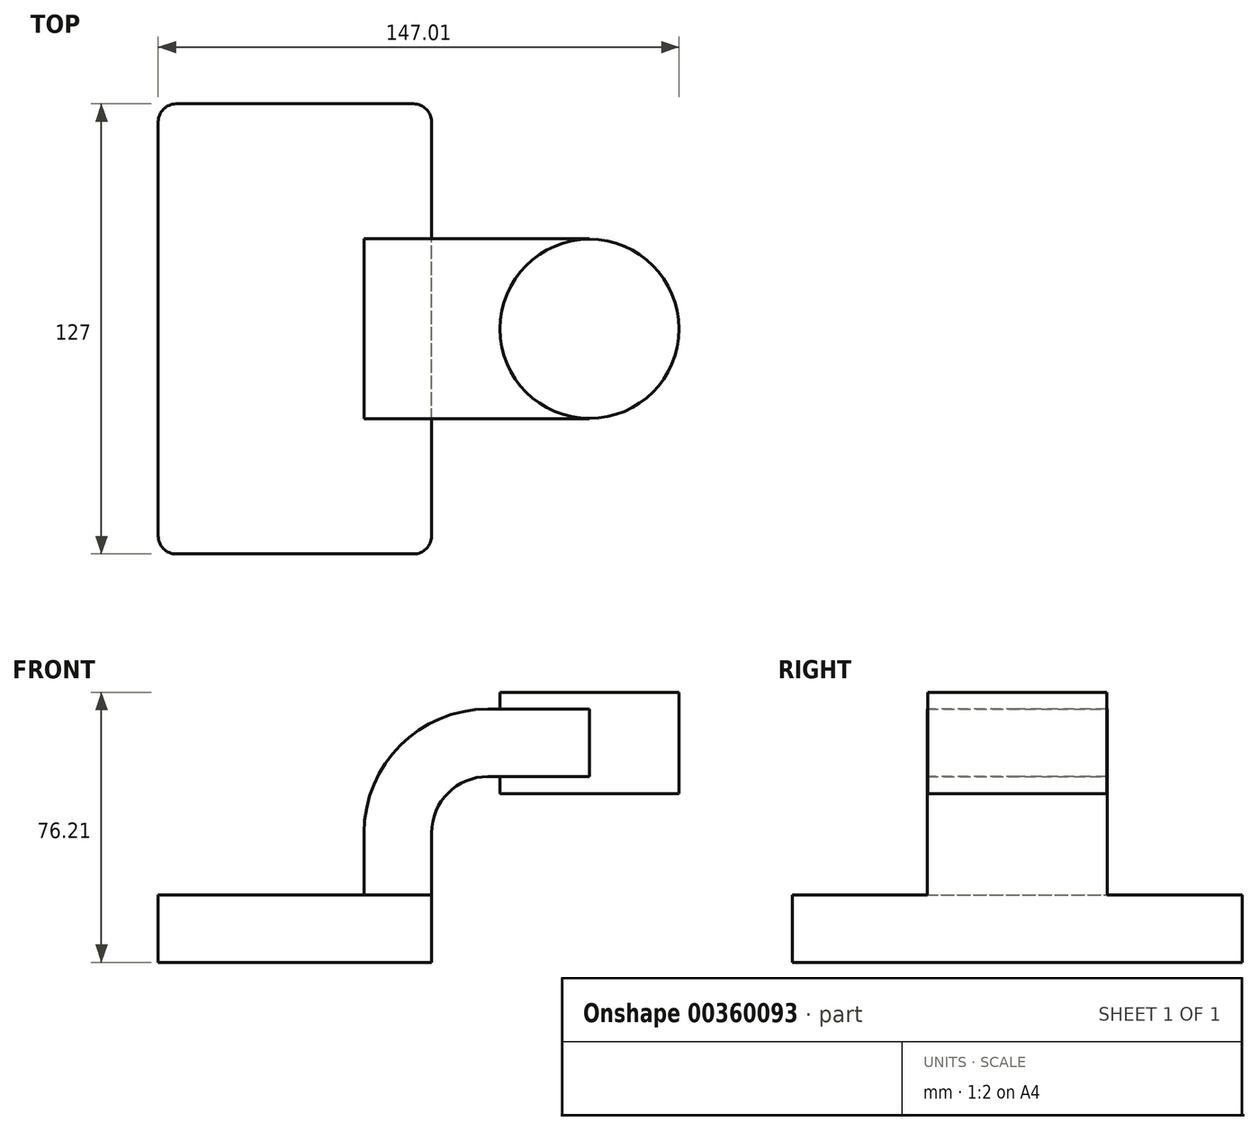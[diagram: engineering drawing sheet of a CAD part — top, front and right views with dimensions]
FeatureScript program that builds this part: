
annotation { "Feature Type Name" : "Feature", "Feature Type Description" : "" }
export const myFeature = defineFeature(function(context is Context, id is Id, definition is map)
    precondition{}
    {
        {
            var Q0;
            Q0=qCreatedBy(makeId("Front.planeOp"),FACE);
            var sketch = newSketch(context, id + "F0", { "sketchPlane" : qUnion([Q0])});
            skLineSegment(sketch, "E0.bottom", {"start": v(-38.58, 9.52) * mm, "end": v(38.58, 9.53) * mm});
            skLineSegment(sketch, "E0.top", {"start": v(-38.58, -9.53) * mm, "end": v(38.58, -9.53) * mm});
            skLineSegment(sketch, "E0.left", {"start": v(-38.58, 9.52) * mm, "end": v(-38.58, -9.53) * mm});
            skLineSegment(sketch, "E0.right", {"start": v(38.58, 9.53) * mm, "end": v(38.58, -9.52) * mm});
            skPoint(sketch, "E0.middle", {"position": v(0, 0) * mm});
            skLineSegment(sketch, "E1.bottom", {"start": v(108.43, 38.1) * mm, "end": v(57.63, 38.1) * mm});
            skLineSegment(sketch, "E1.top", {"start": v(108.43, 66.68) * mm, "end": v(57.63, 66.68) * mm});
            skLineSegment(sketch, "E1.left", {"start": v(108.43, 38.1) * mm, "end": v(108.43, 66.68) * mm});
            skLineSegment(sketch, "E1.right", {"start": v(57.63, 38.1) * mm, "end": v(57.63, 66.68) * mm});
            skPoint(sketch, "E1.middle", {"position": v(83.03, 52.39) * mm});
            skLineSegment(sketch, "E2", {"start": v(38.58, 9.53) * mm, "end": v(38.58, 27) * mm});
            skArc(sketch, "E3", {"start": v(38.58, 27) * mm, "mid": v(43.23, 38.23) * mm, "end": v(54.46, 42.88) * mm});
            skLineSegment(sketch, "E4", {"start": v(54.46, 42.88) * mm, "end": v(83.16, 42.88) * mm});
            skLineSegment(sketch, "E5.0", {"start": v(54.46, 61.93) * mm, "end": v(83.16, 61.93) * mm});
            skArc(sketch, "E5.1", {"start": v(19.53, 27) * mm, "mid": v(29.76, 51.7) * mm, "end": v(54.46, 61.93) * mm});
            skLineSegment(sketch, "E5.2", {"start": v(19.53, 9.53) * mm, "end": v(19.53, 27) * mm});
            skLineSegment(sketch, "E6", {"start": v(83.16, 38.1) * mm, "end": v(83.16, 66.68) * mm});
            skPoint(sketch, "E6.startSnap0", {"position": v(83.03, 38.1) * mm});
            skFitSpline(sketch, "E7", {"points": [v(-38.58, 9.52) * mm, v(54.46, 61.93) * mm], "startDerivative": vector(36.73, 104.26) * mm, "endDerivative": vector(99.66, -5.52) * mm});
            skSolve(sketch);
        }
        {
            var Q0;
            Q0=makeQuery(id+"F0.imprint","IMPRINT",FACE,{"disambiguationData":[TD([[makeQuery(id+"F0.imprint","IMPRINT",EDGE,{"derivedFrom":sQuery(id+"F0.wireOp",EDGE,"E0.top")}),1.0]])]});
            extrude(context, id + "F1", {"entities" : qUnion([Q0]), "endBound" : BoundingType.SYMMETRIC, "depth" : 127 * mm});
        }
        {
            var Q0;
            {var subQ1=sQuery(id+"F0.wireOp",EDGE,"E2");Q0=makeQuery(id+"F0.imprint","IMPRINT",FACE,{"disambiguationData":[TD([[makeQuery(id+"F0.imprint","IMPRINT",EDGE,{"derivedFrom":subQ1}),1.0]])]});}
            var Q1;
            {var subQ0=sQuery(id+"F0.wireOp",EDGE,"E4");var subQ1=sQuery(id+"F0.wireOp",EDGE,"E1.right");var subQ2=makeQuery(id+"F0.imprint","INTERSECT",VERTEX,{"derivedFrom":[subQ1,subQ0]});Q1=makeQuery(id+"F0.imprint","IMPRINT",FACE,{"disambiguationData":[TD([[makeQuery(id+"F0.imprint","IMPRINT",EDGE,{"disambiguationData":[TD([[subQ2,-1.0]])],"derivedFrom":subQ1}),-1.0]])]});}
            extrude(context, id + "F2", {"entities" : qUnion([Q0, Q1]), "operationType" : NewBodyOperationType.ADD, "endBound" : BoundingType.SYMMETRIC, "depth" : 50.8 * mm});
        }
        {
            var Q0;
            Q0=makeQuery(id+"F0.imprint","IMPRINT",FACE,{"disambiguationData":[TD([[makeQuery(id+"F0.imprint","IMPRINT",EDGE,{"derivedFrom":sQuery(id+"F0.wireOp",EDGE,"E5.1")}),1.0]])]});
            extrude(context, id + "F3", {"entities" : qUnion([Q0]), "operationType" : NewBodyOperationType.ADD, "endBound" : BoundingType.SYMMETRIC, "depth" : 15.88 * mm});
        }
        {
            var Q0;
            {var subQ4=sQuery(id+"F0.wireOp",EDGE,"E1.left");Q0=makeQuery(id+"F0.imprint","IMPRINT",FACE,{"disambiguationData":[TD([[makeQuery(id+"F0.imprint","IMPRINT",EDGE,{"derivedFrom":subQ4}),1.0]])]});}
            var Q1;
            Q1=sQuery(id+"F0.wireOp",EDGE,"E6");
            revolve(context, id + "F4", {"operationType" : NewBodyOperationType.ADD, "entities" : qUnion([Q0]), "axis" : qUnion([Q1]), "revolveType" : RevolveType.FULL});
        }
        {
            var Q0;
            Q0=makeQuery(id+"F1.opExtrude","CAP_EDGE",EDGE,{"disambiguationData":[OSD([sQuery(id+"F0.wireOp",EDGE,"E0.right")])],"isStart":false});
            var Q1;
            Q1=makeQuery(id+"F1.opExtrude","CAP_EDGE",EDGE,{"disambiguationData":[OSD([sQuery(id+"F0.wireOp",EDGE,"E0.left")])],"isStart":false});
            var Q2;
            Q2=makeQuery(id+"F1.opExtrude","CAP_EDGE",EDGE,{"disambiguationData":[OSD([sQuery(id+"F0.wireOp",EDGE,"E0.right")])],"isStart":true});
            var Q3;
            Q3=makeQuery(id+"F1.opExtrude","CAP_EDGE",EDGE,{"disambiguationData":[OSD([sQuery(id+"F0.wireOp",EDGE,"E0.left")])],"isStart":true});
            fillet(context, id + "F5", {"entities" : qUnion([Q0, Q1, Q2, Q3]), "radius" : 5.08 * mm, "tangentPropagation" : true, "allowEdgeOverflow" : false});
        }
    });
